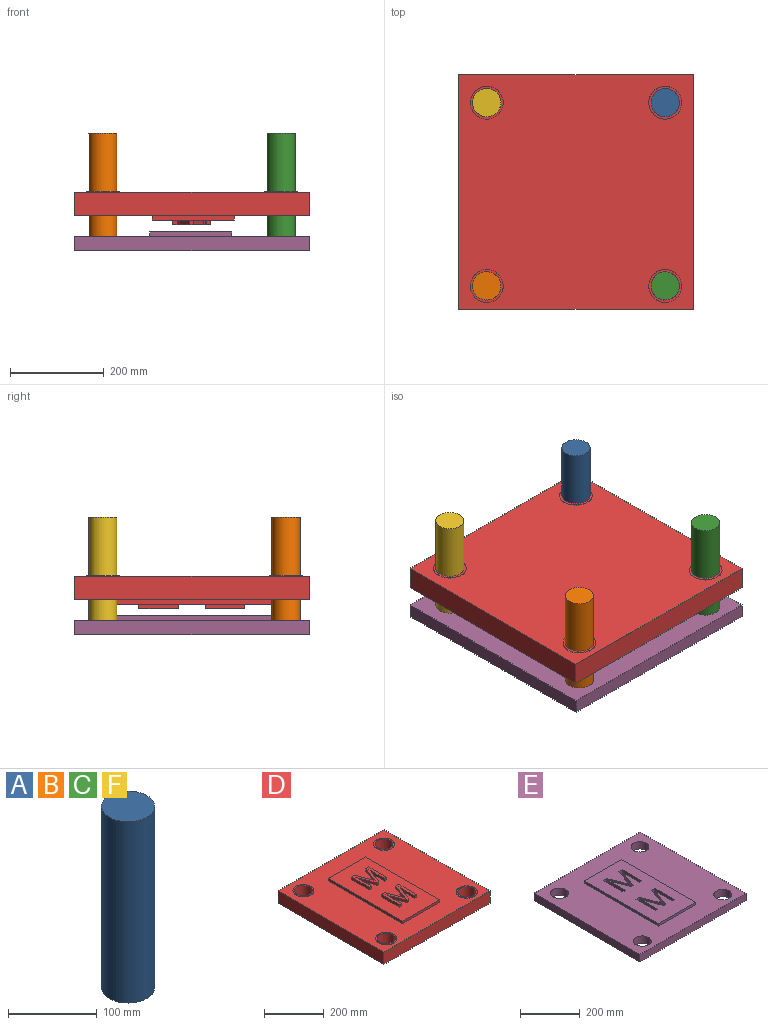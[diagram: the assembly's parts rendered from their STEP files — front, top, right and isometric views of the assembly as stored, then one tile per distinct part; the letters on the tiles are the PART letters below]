
ASSEMBLY  parts=6 mates=5
PART A: 3 faces, bbox 60x60x250 mm
  f0: cylinder r=30mm len=250mm, axis (0,0,-1), area 47123.9mm2, adj f1,f2
  f1: plane 60x60mm, normal (0,0,1), area 2827.4mm2, adj f0
  f2: plane 60x60mm, normal (0,0,-1), area 2827.4mm2, adj f0
PART B: same geometry as A
PART C: same geometry as A
PART D: 79 faces, bbox 500x500x71 mm
  f0: cylinder r=35mm len=66.81mm, axis (0,0,-1), area 5498.4mm2, adj f9,f10,f75
  f1: cylinder r=35mm len=66.81mm, axis (0,0,-1), area 5498.4mm2, adj f9,f10,f64
  f2: plane 350x175mm, normal (0,0,1), area 54796.6mm2, adj f11,f12,f13,f14,f15,f16,f17,f18
  f3: plane 500x50mm, normal (-1,0,0), area 25000mm2, adj f4,f8,f9,f10
  f4: plane 500x50mm, normal (0,-1,0), area 25000mm2, adj f3,f5,f9,f10
  f5: plane 500x50mm, normal (1,0,0), area 25000mm2, adj f4,f8,f9,f10
  f6: cylinder r=35mm len=66.81mm, axis (0,0,-1), area 5498.4mm2, adj f9,f10,f67
  f7: cylinder r=35mm len=66.81mm, axis (0,0,-1), area 5498.4mm2, adj f9,f10,f71
  f8: plane 500x50mm, normal (0,1,0), area 25000mm2, adj f3,f5,f9,f10
  f9: plane 500x500mm, normal (0,0,1), area 173353mm2, adj f0,f1,f3,f4,f5,f6,f7,f8
  f10: plane 500x500mm, normal (0,0,-1), area 234603mm2, adj f0,f1,f3,f4,f5,f6,f7,f8
  f11: plane 175x10mm, normal (0,1,0), area 1750mm2, adj f2,f9,f12,f14
  f12: plane 350x10mm, normal (1,0,0), area 3500mm2, adj f2,f9,f11,f13
  f13: plane 175x10mm, normal (0,-1,0), area 1750mm2, adj f2,f9,f12,f14
  f14: plane 350x10mm, normal (-1,0,0), area 3500mm2, adj f2,f9,f11,f13
  f15: plane 56.38x10mm, normal (-1,0,0), area 563.8mm2, adj f2,f16,f37,f38
  f16: plane 10.3x10mm, normal (0,-1,0), area 103mm2, adj f2,f15,f17,f38
  f17: plane 84.49x10mm, normal (1,0,0), area 844.9mm2, adj f2,f16,f18,f38
  f18: plane 14.68x10mm, normal (0,1,0), area 146.8mm2, adj f2,f17,f19,f38
  f19: plane 58.58x22.07mm, normal (-0.94,0.35,0), area 626mm2, adj f2,f18,f20,f38
  f20: extruded ~10x6.15mm, area 64.9mm2, adj f2,f19,f21,f38
  f21: extruded ~10x7.28mm, area 75.6mm2, adj f2,f20,f22,f38
  f22: extruded ~10x5.85mm, area 60.3mm2, adj f2,f21,f23,f38
  f23: extruded ~10x7.58mm, area 79.3mm2, adj f2,f22,f24,f38
  f24: plane 58.58x22.49mm, normal (0.93,0.36,0), area 627.5mm2, adj f2,f23,f25,f38
  f25: plane 15.04x10mm, normal (0,1,0), area 150.4mm2, adj f2,f24,f26,f38
  f26: plane 84.49x10mm, normal (-1,0,0), area 844.9mm2, adj f2,f25,f27,f38
  f27: plane 10.19x10mm, normal (0,-1,0), area 101.9mm2, adj f2,f26,f28,f38
  f28: plane 56.38x10mm, normal (1,0,0), area 563.8mm2, adj f2,f27,f29,f38
  f29: plane 11.32x10mm, normal (1,0.02,0), area 113.2mm2, adj f2,f28,f30,f38
  f30: plane 10x6.66mm, normal (1,0.03,0), area 66.6mm2, adj f2,f29,f31,f38
  f31: plane 10x6.6mm, normal (-0.96,-0.29,0), area 69mm2, adj f2,f30,f32,f38
  f32: plane 10.19x10mm, normal (-0.95,-0.31,0), area 107.3mm2, adj f2,f31,f33,f38
  f33: plane 57.57x22.12mm, normal (-0.93,-0.36,0), area 616.7mm2, adj f2,f32,f34,f38
  f34: plane 10x8.02mm, normal (0,-1,0), area 80.2mm2, adj f2,f33,f35,f38
  f35: plane 57.57x21.84mm, normal (0.93,-0.35,0), area 615.7mm2, adj f2,f34,f36,f38
  f36: extruded ~16.79x10mm, area 176.1mm2, adj f2,f35,f37,f38
  f37: extruded ~17.98x10mm, area 179.9mm2, adj f2,f15,f36,f38
  f38: plane 84.49x82.15mm, normal (0,0,1), area 3226.7mm2, adj f15,f16,f17,f18,f19,f20,f21,f22
  f39: plane 56.38x10mm, normal (-1,0,0), area 563.8mm2, adj f2,f40,f61,f62
  f40: plane 10.3x10mm, normal (0,-1,0), area 103mm2, adj f2,f39,f41,f62
  f41: plane 84.49x10mm, normal (1,0,0), area 844.9mm2, adj f2,f40,f42,f62
  f42: plane 14.68x10mm, normal (0,1,0), area 146.8mm2, adj f2,f41,f43,f62
  f43: plane 58.58x22.07mm, normal (-0.94,0.35,0), area 626mm2, adj f2,f42,f44,f62
  f44: extruded ~10x6.15mm, area 64.9mm2, adj f2,f43,f45,f62
  f45: extruded ~10x7.28mm, area 75.6mm2, adj f2,f44,f46,f62
  f46: extruded ~10x5.85mm, area 60.3mm2, adj f2,f45,f47,f62
  f47: extruded ~10x7.58mm, area 79.3mm2, adj f2,f46,f48,f62
  f48: plane 58.58x22.49mm, normal (0.93,0.36,0), area 627.5mm2, adj f2,f47,f49,f62
  f49: plane 15.04x10mm, normal (0,1,0), area 150.4mm2, adj f2,f48,f50,f62
  f50: plane 84.49x10mm, normal (-1,0,0), area 844.9mm2, adj f2,f49,f51,f62
  f51: plane 10.19x10mm, normal (0,-1,0), area 101.9mm2, adj f2,f50,f52,f62
  f52: plane 56.38x10mm, normal (1,0,0), area 563.8mm2, adj f2,f51,f53,f62
  f53: plane 11.32x10mm, normal (1,0.02,0), area 113.2mm2, adj f2,f52,f54,f62
  f54: plane 10x6.66mm, normal (1,0.03,0), area 66.6mm2, adj f2,f53,f55,f62
  f55: plane 10x6.6mm, normal (-0.96,-0.29,0), area 69mm2, adj f2,f54,f56,f62
  f56: plane 10.19x10mm, normal (-0.95,-0.31,0), area 107.3mm2, adj f2,f55,f57,f62
  f57: plane 57.57x22.12mm, normal (-0.93,-0.36,0), area 616.7mm2, adj f2,f56,f58,f62
  f58: plane 10x8.02mm, normal (0,-1,0), area 80.2mm2, adj f2,f57,f59,f62
  f59: plane 57.57x21.84mm, normal (0.93,-0.35,0), area 615.7mm2, adj f2,f58,f60,f62
  f60: extruded ~16.79x10mm, area 176.1mm2, adj f2,f59,f61,f62
  f61: extruded ~17.98x10mm, area 179.9mm2, adj f2,f39,f60,f62
  f62: plane 84.49x82.15mm, normal (0,0,1), area 3226.7mm2, adj f39,f40,f41,f42,f43,f44,f45,f46
  f63: cylinder r=30mm len=60mm, axis (0,0,-1), area 9801.8mm2, adj f65,f66
  f64: cylinder r=35mm len=70mm, axis (0,0,-1), area 5937mm2, adj f1,f9,f10,f65,f66
  f65: plane 70x70mm, normal (0,0,1), area 1021mm2, adj f63,f64
  f66: plane 70x70mm, normal (0,0,-1), area 1021mm2, adj f63,f64
  f67: cylinder r=35mm len=70mm, axis (0,0,-1), area 5937mm2, adj f6,f9,f10,f69,f70
  f68: cylinder r=30mm len=60mm, axis (0,0,-1), area 9801.8mm2, adj f69,f70
  f69: plane 70x70mm, normal (0,0,1), area 1021mm2, adj f67,f68
  f70: plane 70x70mm, normal (0,0,-1), area 1021mm2, adj f67,f68
  f71: cylinder r=35mm len=70mm, axis (0,0,-1), area 5937mm2, adj f7,f9,f10,f73,f74
  f72: cylinder r=30mm len=60mm, axis (0,0,-1), area 9801.8mm2, adj f73,f74
  f73: plane 70x70mm, normal (0,0,1), area 1021mm2, adj f71,f72
  f74: plane 70x70mm, normal (0,0,-1), area 1021mm2, adj f71,f72
  f75: cylinder r=35mm len=70mm, axis (0,0,-1), area 5937mm2, adj f0,f9,f10,f77,f78
  f76: cylinder r=30mm len=60mm, axis (0,0,-1), area 9801.8mm2, adj f77,f78
  f77: plane 70x70mm, normal (0,0,1), area 1021mm2, adj f75,f76
  f78: plane 70x70mm, normal (0,0,-1), area 1021mm2, adj f75,f76
PART E: 61 faces, bbox 500x500x40 mm
  f0: plane 500x30mm, normal (-1,0,0), area 15000mm2, adj f1,f7,f8,f9
  f1: plane 500x30mm, normal (0,-1,0), area 15000mm2, adj f0,f2,f8,f9
  f2: plane 500x30mm, normal (1,0,0), area 15000mm2, adj f1,f7,f8,f9
  f3: cylinder r=30mm len=60mm, axis (0,0,-1), area 5654.9mm2, adj f8,f9
  f4: cylinder r=30mm len=60mm, axis (0,0,-1), area 5654.9mm2, adj f8,f9
  f5: cylinder r=30mm len=60mm, axis (0,0,-1), area 5654.9mm2, adj f8,f9
  f6: cylinder r=30mm len=60mm, axis (0,0,-1), area 5654.9mm2, adj f8,f9
  f7: plane 500x30mm, normal (0,1,0), area 15000mm2, adj f0,f2,f8,f9
  f8: plane 500x500mm, normal (0,0,1), area 177440.3mm2, adj f0,f1,f2,f3,f4,f5,f6,f7
  f9: plane 500x500mm, normal (0,0,-1), area 231049.6mm2, adj f0,f1,f2,f3,f4,f5,f6,f7
  f10: plane 40x11.21mm, normal (0,1,0), area 448.5mm2, adj f9,f11,f59,f60
  f11: plane 61.34x40mm, normal (1,0,0), area 2453.7mm2, adj f9,f10,f12,f60
  f12: extruded ~40x19.56mm, area 783mm2, adj f9,f11,f13,f60
  f13: extruded ~40x18.27mm, area 766.3mm2, adj f9,f12,f14,f60
  f14: plane 62.64x40mm, normal (-0.93,0.35,0), area 2679.7mm2, adj f9,f13,f15,f60
  f15: plane 40x8.73mm, normal (0,1,0), area 349.1mm2, adj f9,f14,f16,f60
  f16: plane 62.64x40mm, normal (0.93,0.36,0), area 2684.2mm2, adj f9,f15,f17,f60
  f17: plane 40x11.09mm, normal (0.95,0.31,0), area 466.9mm2, adj f9,f16,f18,f60
  f18: plane 40x7.18mm, normal (0.96,0.29,0), area 300.1mm2, adj f9,f17,f19,f60
  f19: plane 40x7.25mm, normal (-1,-0.03,0), area 289.9mm2, adj f9,f18,f20,f60
  f20: plane 40x12.32mm, normal (-1,-0.02,0), area 492.8mm2, adj f9,f19,f21,f60
  f21: plane 61.34x40mm, normal (-1,0,0), area 2453.7mm2, adj f9,f20,f22,f60
  f22: plane 40x11.09mm, normal (0,1,0), area 443.5mm2, adj f9,f21,f23,f60
  f23: plane 91.93x40mm, normal (1,0,0), area 3677.2mm2, adj f9,f22,f24,f60
  f24: plane 40x16.37mm, normal (0,-1,0), area 654.8mm2, adj f9,f23,f25,f60
  f25: plane 63.74x40mm, normal (-0.93,-0.36,0), area 2731.2mm2, adj f9,f24,f26,f60
  f26: extruded ~40x8.25mm, area 345mm2, adj f9,f25,f27,f60
  f27: extruded ~40x6.37mm, area 262.7mm2, adj f9,f26,f28,f60
  f28: extruded ~40x7.92mm, area 329mm2, adj f9,f27,f29,f60
  f29: extruded ~40x6.69mm, area 282.5mm2, adj f9,f28,f30,f60
  f30: plane 63.74x40mm, normal (0.94,-0.35,0), area 2724.6mm2, adj f9,f29,f31,f60
  f31: plane 40x15.97mm, normal (0,-1,0), area 638.9mm2, adj f9,f30,f59,f60
  f32: plane 40x11.21mm, normal (0,1,0), area 448.5mm2, adj f9,f33,f57,f60
  f33: plane 61.34x40mm, normal (1,0,0), area 2453.7mm2, adj f9,f32,f34,f60
  f34: extruded ~40x19.56mm, area 783mm2, adj f9,f33,f35,f60
  f35: extruded ~40x18.27mm, area 766.3mm2, adj f9,f34,f36,f60
  f36: plane 62.64x40mm, normal (-0.93,0.35,0), area 2679.7mm2, adj f9,f35,f37,f60
  f37: plane 40x8.73mm, normal (0,1,0), area 349.1mm2, adj f9,f36,f38,f60
  f38: plane 62.64x40mm, normal (0.93,0.36,0), area 2684.2mm2, adj f9,f37,f39,f60
  f39: plane 40x11.09mm, normal (0.95,0.31,0), area 466.9mm2, adj f9,f38,f40,f60
  f40: plane 40x7.18mm, normal (0.96,0.29,0), area 300.1mm2, adj f9,f39,f41,f60
  f41: plane 40x7.25mm, normal (-1,-0.03,0), area 289.9mm2, adj f9,f40,f42,f60
  f42: plane 40x12.32mm, normal (-1,-0.02,0), area 492.8mm2, adj f9,f41,f43,f60
  f43: plane 61.34x40mm, normal (-1,0,0), area 2453.7mm2, adj f9,f42,f44,f60
  f44: plane 40x11.09mm, normal (0,1,0), area 443.5mm2, adj f9,f43,f45,f60
  f45: plane 91.93x40mm, normal (1,0,0), area 3677.2mm2, adj f9,f44,f46,f60
  f46: plane 40x16.37mm, normal (0,-1,0), area 654.8mm2, adj f9,f45,f47,f60
  f47: plane 63.74x40mm, normal (-0.93,-0.36,0), area 2731.2mm2, adj f9,f46,f48,f60
  f48: extruded ~40x8.25mm, area 345mm2, adj f9,f47,f49,f60
  f49: extruded ~40x6.37mm, area 262.7mm2, adj f9,f48,f50,f60
  f50: extruded ~40x7.92mm, area 329mm2, adj f9,f49,f51,f60
  f51: extruded ~40x6.69mm, area 282.5mm2, adj f9,f50,f52,f60
  f52: plane 63.74x40mm, normal (0.94,-0.35,0), area 2724.6mm2, adj f9,f51,f53,f60
  f53: plane 40x15.97mm, normal (0,-1,0), area 638.9mm2, adj f9,f52,f57,f60
  f54: plane 350x10mm, normal (-1,0,0), area 3500mm2, adj f8,f55,f58,f60
  f55: plane 175x10mm, normal (0,-1,0), area 1750mm2, adj f8,f54,f56,f60
  f56: plane 350x10mm, normal (1,0,0), area 3500mm2, adj f8,f55,f58,f60
  f57: plane 91.93x40mm, normal (-1,0,0), area 3677.2mm2, adj f9,f32,f53,f60
  f58: plane 175x10mm, normal (0,1,0), area 1750mm2, adj f8,f54,f56,f60
  f59: plane 91.93x40mm, normal (-1,0,0), area 3677.2mm2, adj f9,f10,f31,f60
  f60: plane 350x175mm, normal (0,0,1), area 53609.3mm2, adj f10,f11,f12,f13,f14,f15,f16,f17
PART F: same geometry as A
PLACE A t=(255.05,211.69,-43.8)mm
PLACE B t=(-124.95,-178.67,-43.8)mm
PLACE C t=(255.05,-178.67,-43.8)mm
PLACE D rot(axis=(0,1,0),180deg) t=(65.05,16.51,81.2)mm
PLACE E t=(65.05,16.51,-43.8)mm
PLACE F t=(-124.95,211.69,-43.8)mm
MATE fastened C.f0 <-> E.f5  axis (0,0,-1) through (255.05,-178.67,-43.8)mm
MATE fastened B.f0 <-> E.f4  axis (0,0,-1) through (-124.95,-178.67,-43.8)mm
MATE fastened F.f0 <-> E.f3  axis (0,0,-1) through (-124.95,211.69,-43.8)mm
MATE fastened A.f0 <-> E.f6  axis (0,0,-1) through (255.05,211.69,-43.8)mm
MATE slider D.f6 <-> B.f0  axis (0,0,1) through (-124.95,-178.67,81.2)mm
